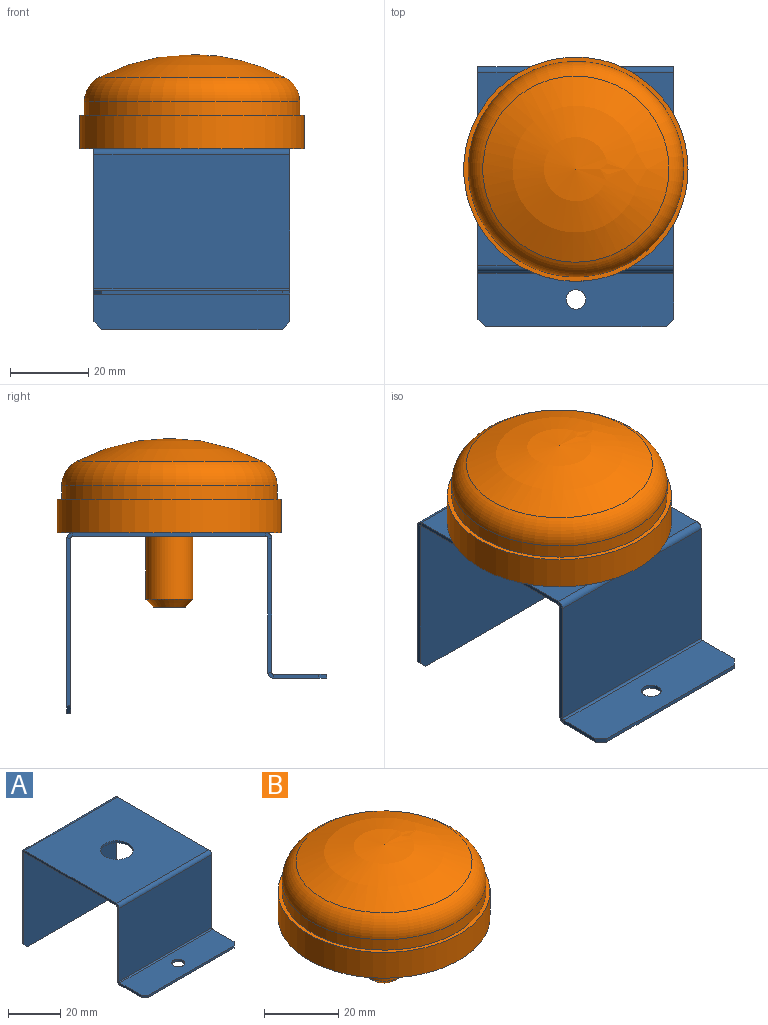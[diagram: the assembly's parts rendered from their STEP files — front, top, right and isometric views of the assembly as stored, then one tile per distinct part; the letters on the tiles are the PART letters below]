
ASSEMBLY  parts=2 mates=1
PART A: 36 faces, bbox 50x66.3x46.1 mm
  f0: plane 49.29x1mm, normal (1,0,0), area 49.3mm2, adj f3,f4,f22,f33
  f1: plane 49.29x1mm, normal (-1,0,0), area 49.3mm2, adj f3,f4,f21,f32
  f2: cylinder r=6.2mm len=12.4mm, axis (0,0,1), area 39mm2, adj f3,f4
  f3: plane 50x49.29mm, normal (0,0,1), area 2343.9mm2, adj f0,f1,f2,f23,f34
  f4: plane 50x49.29mm, normal (0,0,-1), area 2343.9mm2, adj f0,f1,f2,f24,f35
  f5: plane 34.15x1mm, normal (1,0,0), area 34.1mm2, adj f7,f8,f18,f22
  f6: plane 34.15x1mm, normal (-1,0,0), area 34.1mm2, adj f7,f8,f17,f21
  f7: plane 50x34.15mm, normal (0,-1,0), area 1707.3mm2, adj f5,f6,f20,f23
  f8: plane 50x34.15mm, normal (0,1,0), area 1707.3mm2, adj f5,f6,f19,f24
  f9: plane 46x1mm, normal (0,-1,0), area 46mm2, adj f13,f14,f15,f16
  f10: plane 11.5x1mm, normal (1,0,0), area 11.5mm2, adj f13,f14,f15,f18
  f11: cylinder r=2.5mm len=5mm, axis (0,0,1), area 15.7mm2, adj f13,f14
  f12: plane 11.5x1mm, normal (-1,0,0), area 11.5mm2, adj f13,f14,f16,f17
  f13: plane 50x13.5mm, normal (0,0,1), area 651.4mm2, adj f9,f10,f11,f12,f15,f16,f20
  f14: plane 50x13.5mm, normal (0,0,-1), area 651.4mm2, adj f9,f10,f11,f12,f15,f16,f19
  f15: plane 2x2mm, normal (0.71,-0.71,0), area 2.8mm2, adj f9,f10,f13,f14
  f16: plane 2x2mm, normal (-0.71,-0.71,0), area 2.8mm2, adj f9,f12,f13,f14
  f17: plane 1.5x1.5mm, normal (-1,0,0), area 1.6mm2, adj f6,f12,f19,f20
  f18: plane 1.5x1.5mm, normal (1,0,0), area 1.6mm2, adj f5,f10,f19,f20
  f19: cylinder r=1.5mm len=50mm, axis (-1,0,0), area 117.8mm2, adj f8,f14,f17,f18
  f20: cylinder r=0.5mm len=50mm, axis (-1,0,0), area 39.3mm2, adj f7,f13,f17,f18
  f21: plane 1.5x1.5mm, normal (-1,0,0), area 1.6mm2, adj f1,f6,f23,f24
  f22: plane 1.5x1.5mm, normal (1,0,0), area 1.6mm2, adj f0,f5,f23,f24
  f23: cylinder r=1.5mm len=50mm, axis (-1,0,0), area 117.8mm2, adj f3,f7,f21,f22
  f24: cylinder r=0.5mm len=50mm, axis (-1,0,0), area 39.3mm2, adj f4,f8,f21,f22
  f25: plane 42.65x1mm, normal (1,0,0), area 42.6mm2, adj f28,f29,f30,f33
  f26: plane 46x1mm, normal (0,0,-1), area 46mm2, adj f28,f29,f30,f31
  f27: plane 42.65x1mm, normal (-1,0,0), area 42.6mm2, adj f28,f29,f31,f32
  f28: plane 50x44.65mm, normal (0,1,0), area 2228.3mm2, adj f25,f26,f27,f30,f31,f34
  f29: plane 50x44.65mm, normal (0,-1,0), area 2228.3mm2, adj f25,f26,f27,f30,f31,f35
  f30: plane 2x2mm, normal (0.71,0,-0.71), area 2.8mm2, adj f25,f26,f28,f29
  f31: plane 2x2mm, normal (-0.71,0,-0.71), area 2.8mm2, adj f26,f27,f28,f29
  f32: plane 1.5x1.5mm, normal (-1,0,0), area 1.6mm2, adj f1,f27,f34,f35
  f33: plane 1.5x1.5mm, normal (1,0,0), area 1.6mm2, adj f0,f25,f34,f35
  f34: cylinder r=1.5mm len=50mm, axis (-1,0,0), area 117.8mm2, adj f3,f28,f32,f33
  f35: cylinder r=0.5mm len=50mm, axis (-1,0,0), area 39.3mm2, adj f4,f29,f32,f33
PART B: 9 faces, bbox 59.5x59.5x43 mm
  f0: cylinder r=6mm len=17mm, axis (0,0,1), area 640.9mm2, adj f7,f8
  f1: plane 8x8mm, normal (0,0,-1), area 50.3mm2, adj f8
  f2: sphere r=51.14mm, area 1879.8mm2, adj f3
  f3: torus R=20.5mm, axis (0,0,1), area 1253.4mm2, adj f2,f4
  f4: cylinder r=27.5mm len=55mm, axis (0,0,1), area 600.3mm2, adj f3,f5
  f5: plane 57.22x57.22mm, normal (0,0,1), area 195.7mm2, adj f4,f6
  f6: cylinder r=28.61mm len=57.22mm, axis (0,0,1), area 1528mm2, adj f5,f7
  f7: plane 57.22x57.22mm, normal (0,0,-1), area 2458.4mm2, adj f0,f6
  f8: cone r=6mm half-angle=45deg, axis (0,0,1), area 88.9mm2, adj f0,f1
PLACE A at identity fixed
PLACE B t=(0,0,23.65)mm
MATE fastened B.f0 <-> A.f2  axis (0,0,1) through (0,0,23.65)mm
